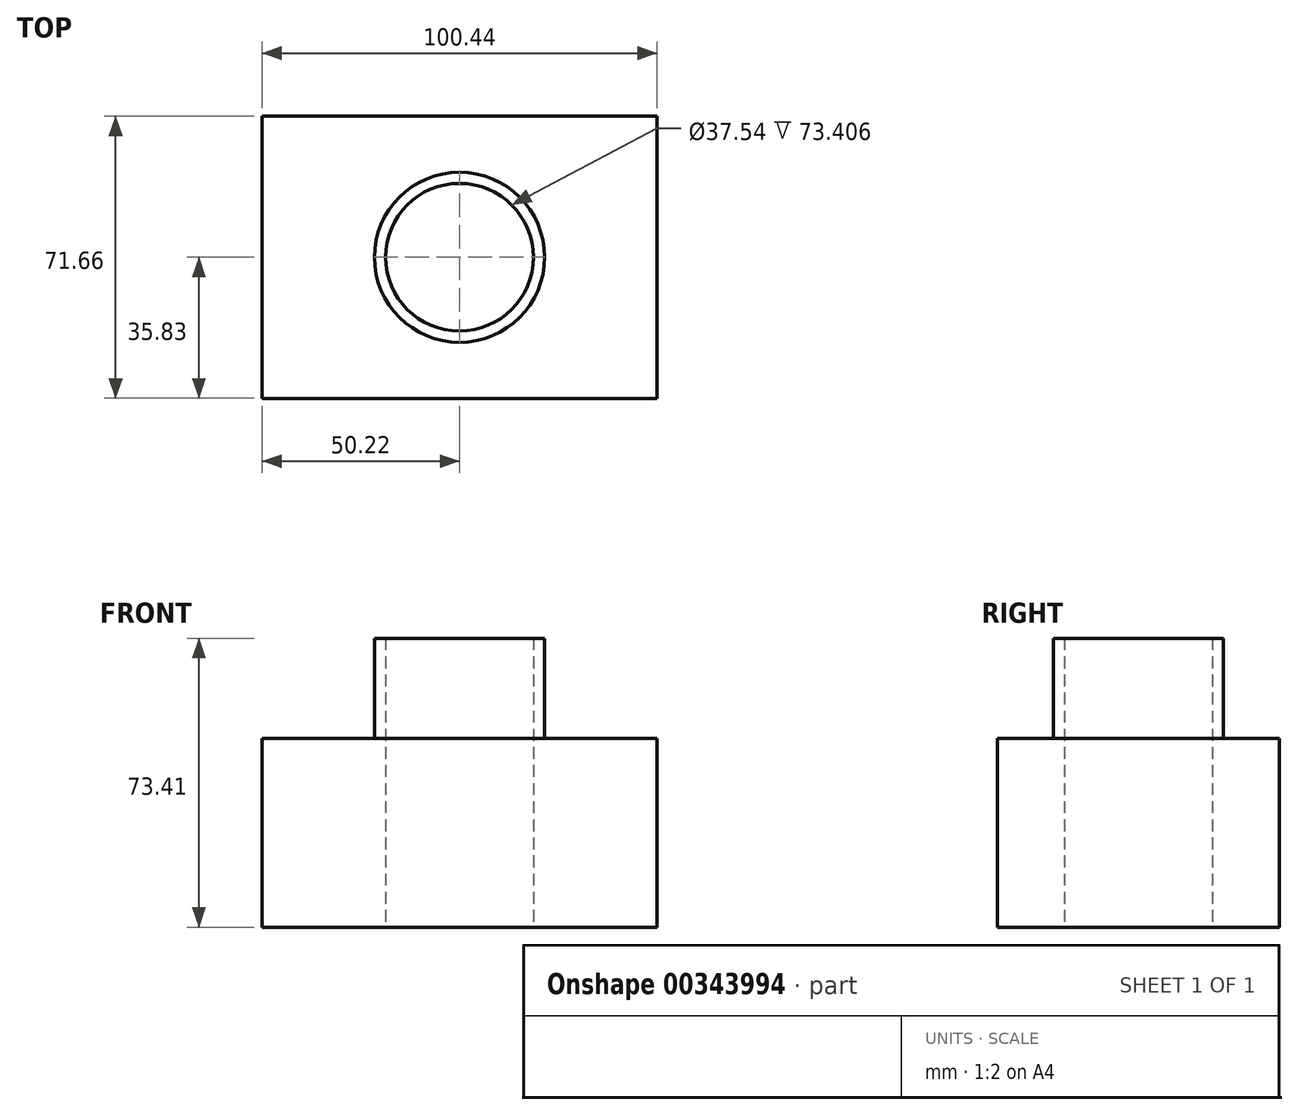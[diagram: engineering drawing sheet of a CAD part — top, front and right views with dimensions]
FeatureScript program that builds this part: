
annotation { "Feature Type Name" : "Feature", "Feature Type Description" : "" }
export const myFeature = defineFeature(function(context is Context, id is Id, definition is map)
    precondition{}
    {
        {
            var Q0;
            Q0=qCreatedBy(makeId("Top.planeOp"),FACE);
            var sketch = newSketch(context, id + "F0", { "sketchPlane" : qUnion([Q0])});
            skLineSegment(sketch, "E0.bottom", {"start": v(50.22, 35.83) * mm, "end": v(-50.22, 35.83) * mm});
            skLineSegment(sketch, "E0.top", {"start": v(50.22, -35.83) * mm, "end": v(-50.22, -35.83) * mm});
            skLineSegment(sketch, "E0.left", {"start": v(50.22, 35.83) * mm, "end": v(50.22, -35.83) * mm});
            skLineSegment(sketch, "E0.right", {"start": v(-50.22, 35.83) * mm, "end": v(-50.22, -35.83) * mm});
            skPoint(sketch, "E0.middle", {"position": v(0, 0) * mm});
            skSolve(sketch);
        }
        {
            var Q0;
            Q0=makeQuery(id+"F0.imprint","IMPRINT",FACE,{"disambiguationData":[TD([[makeQuery(id+"F0.imprint","IMPRINT",EDGE,{"derivedFrom":sQuery(id+"F0.wireOp",EDGE,"E0.bottom")}),1.0]])]});
            extrude(context, id + "F1", {"entities" : qUnion([Q0]), "depth" : 48 * mm});
        }
        {
            var Q0;
            Q0=makeQuery(id+"F1.opExtrude","CAP_FACE",FACE,{"disambiguationData":[OSD([sQuery(id+"F0.wireOp",EDGE,"E0.bottom"),sQuery(id+"F0.wireOp",EDGE,"E0.top"),sQuery(id+"F0.wireOp",EDGE,"E0.left"),sQuery(id+"F0.wireOp",EDGE,"E0.right")])],"isStart":false});
            var sketch = newSketch(context, id + "F2", { "sketchPlane" : qUnion([Q0])});
            skCircle(sketch, "E1", {"center": v(0, 0) * mm, "radius": 21.61 * mm});
            skCircle(sketch, "E2", {"center": v(0, 0) * mm, "radius": 18.77 * mm});
            skSolve(sketch);
        }
        {
            var Q0;
            Q0=makeQuery(id+"F2.imprint","IMPRINT",FACE,{"disambiguationData":[TD([[makeQuery(id+"F2.imprint","IMPRINT",EDGE,{"derivedFrom":sQuery(id+"F2.wireOp",EDGE,"E1")}),1.0]])]});
            extrude(context, id + "F3", {"entities" : qUnion([Q0]), "operationType" : NewBodyOperationType.ADD, "depth" : 25.4 * mm});
        }
        {
            var Q0;
            Q0=makeQuery(id+"F3.boolean.opBoolean","SPLIT",FACE,{"disambiguationData":[TD([makeQuery(id+"F3.opExtrude","SWEPT_FACE",FACE,{"disambiguationData":[OSD([sQuery(id+"F2.wireOp",EDGE,"E2")])]})])],"derivedFrom":makeQuery(id+"F1.opExtrude","CAP_FACE",FACE,{"disambiguationData":[OSD([sQuery(id+"F0.wireOp",EDGE,"E0.bottom"),sQuery(id+"F0.wireOp",EDGE,"E0.top"),sQuery(id+"F0.wireOp",EDGE,"E0.left"),sQuery(id+"F0.wireOp",EDGE,"E0.right")])],"isStart":false})});
            extrude(context, id + "F4", {"entities" : qUnion([Q0]), "operationType" : NewBodyOperationType.REMOVE, "oppositeDirection" : true, "depth" : 86.36 * mm});
        }
    });
